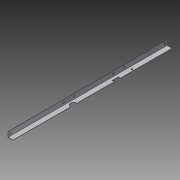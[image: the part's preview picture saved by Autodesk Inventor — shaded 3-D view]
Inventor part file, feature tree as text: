
AUTODESK INVENTOR PART (.ipt)
format: ipt  version: 2014 SP1 (Build 180222100, 222)  size: 160,768 bytes
history: native  units: in
note: dims shown in document units (in); Inventor stores cm internally (conversion verified against a paired STEP export)
features: reference x6, extrude x3, sketch x3
ambient origin geometry x8: Origin, YZ Plane, XZ Plane, XY Plane, X Axis, Y Axis, Z Axis, Center Point
bodies: Solid1 (feature_tree)
feature tree (12):
  extrude  "Extrusion1"  Depth=0.0312in
  extrude  "Extrusion2"  Depth=0.25in
  extrude  "Extrusion3"  Depth=0.0312in TaperAngle=0.0deg
  sketch  "Sketch1"  dims[d0=0.625in d1=0.0312in]
  sketch  "Sketch2"  dims[d2=19.5in d3=0.0in d4=0.25in]
  reference  "Reference1"
  sketch  "Sketch3"  dims[d5=0.75in d6=1.0in d7=0.0in d8=0.125in d9=0.0312in d10=0.0312in d11=0.0312in d12=0.0312in d13=1.0in d14=0.0in]
  reference  "Reference2"
  reference  "Reference3"
  reference  "Reference4"
  reference  "Reference5"
  reference  "Reference6"
